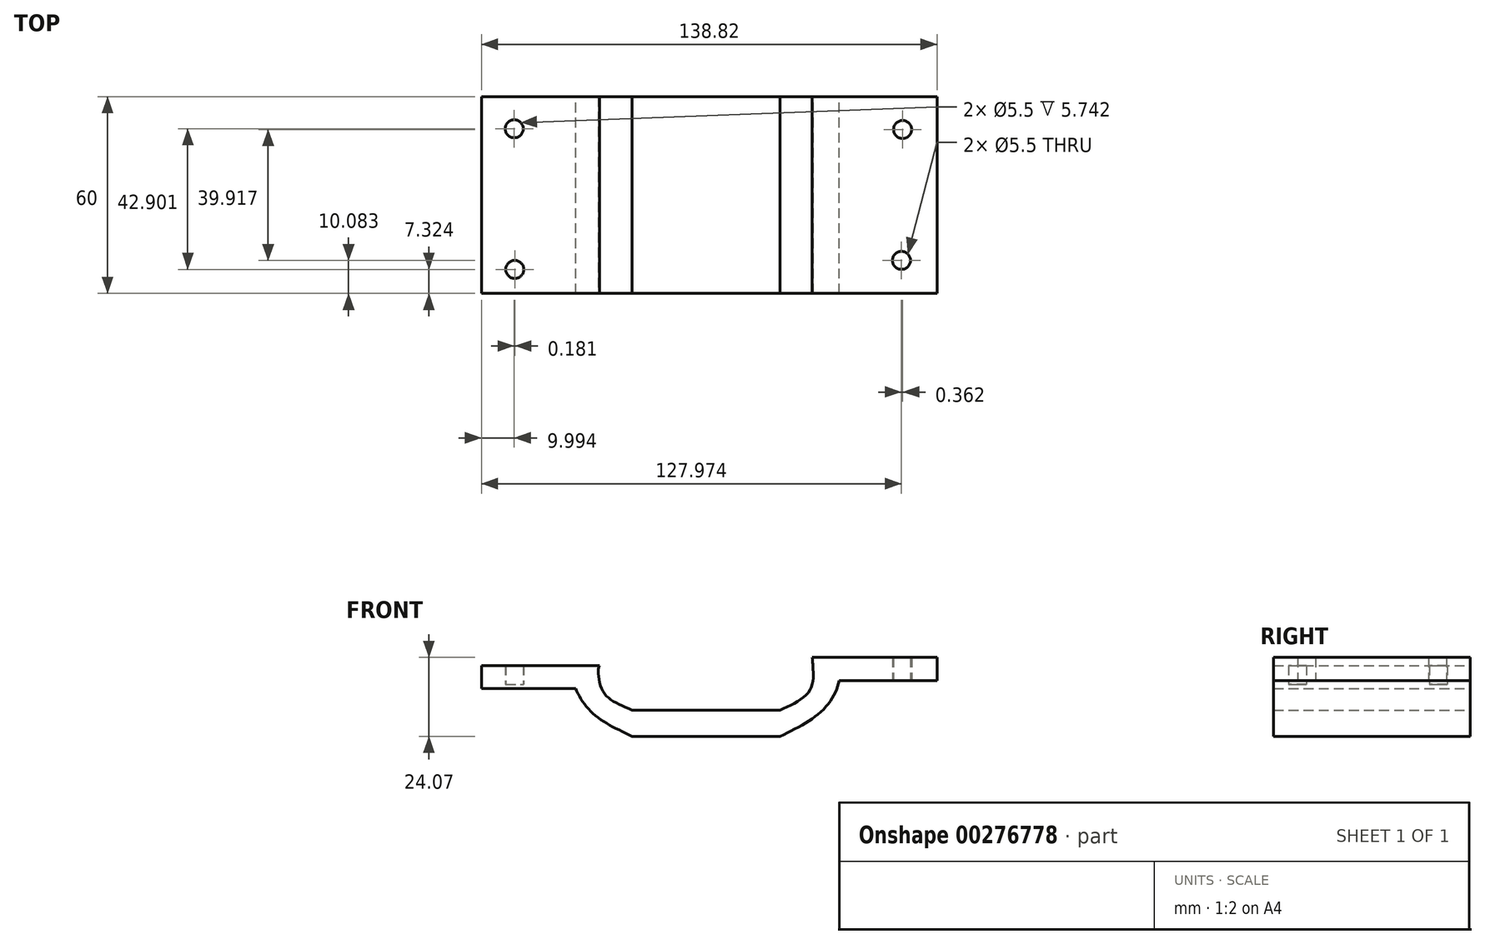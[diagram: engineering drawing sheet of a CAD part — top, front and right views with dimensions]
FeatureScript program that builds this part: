
annotation { "Feature Type Name" : "Feature", "Feature Type Description" : "" }
export const myFeature = defineFeature(function(context is Context, id is Id, definition is map)
    precondition{}
    {
        {
            var Q0;
            Q0=qCreatedBy(makeId("Front.planeOp"),FACE);
            var sketch = newSketch(context, id + "F0", { "sketchPlane" : qUnion([Q0])});
            skPoint(sketch, "E0.middle", {"position": v(20.36, 1.19) * mm});
            skLineSegment(sketch, "E1", {"start": v(-15.58, -15.88) * mm, "end": v(29.42, -15.88) * mm});
            skLineSegment(sketch, "E2", {"start": v(-25.58, 5.74) * mm, "end": v(-33.58, 5.74) * mm});
            skFitSpline(sketch, "E3", {"points": [v(-15.58, -15.88) * mm, v(-28.58, -7.88) * mm, v(-33.58, 1.19) * mm, v(-33.58, 5.74) * mm], "startDerivative": vector(-35.54, 17.11) * mm, "endDerivative": vector(2.54, 22.06) * mm});
            skFitSpline(sketch, "E4", {"points": [v(29.42, -15.88) * mm, v(42.42, -7.88) * mm, v(47.42, 1.19) * mm, v(47.28, 8.19) * mm], "startDerivative": vector(35.54, 17.11) * mm, "endDerivative": vector(-2.54, 22.06) * mm});
            skFitSpline(sketch, "E5", {"points": [v(-25.58, 5.74) * mm, v(-25.8, 5.24) * mm, v(-24.65, -1.83) * mm, v(-15.58, -7.88) * mm], "startDerivative": vector(-1.25, -8.06) * mm, "endDerivative": vector(24.82, -10.78) * mm});
            skLineSegment(sketch, "E6", {"start": v(47.28, 8.19) * mm, "end": v(39.28, 8.19) * mm});
            skFitSpline(sketch, "E7", {"points": [v(39.28, 8.19) * mm, v(39.5, 5.24) * mm, v(38.5, -1.83) * mm, v(29.42, -7.88) * mm], "startDerivative": vector(1.15, -8.05) * mm, "endDerivative": vector(-25.06, -10.75) * mm});
            skLineSegment(sketch, "E8", {"start": v(-15.58, -7.88) * mm, "end": v(29.42, -7.88) * mm});
            skLineSegment(sketch, "E9", {"start": v(47.28, 8.19) * mm, "end": v(77.28, 8.19) * mm});
            skLineSegment(sketch, "E10", {"start": v(77.28, 8.19) * mm, "end": v(77.28, 1.19) * mm});
            skLineSegment(sketch, "E11", {"start": v(77.28, 1.19) * mm, "end": v(47.42, 1.19) * mm});
            skLineSegment(sketch, "E12", {"start": v(-33.58, 5.74) * mm, "end": v(-61.54, 5.74) * mm});
            skLineSegment(sketch, "E13", {"start": v(-61.54, 5.74) * mm, "end": v(-61.54, -1.26) * mm});
            skLineSegment(sketch, "E14", {"start": v(-61.54, -1.26) * mm, "end": v(-32.82, -1.26) * mm});
            skLineSegment(sketch, "E15", {"start": v(-64.92, 5.46) * mm, "end": v(-64.92, -15.43) * mm});
            skSolve(sketch);
        }
        {
            var Q0;
            Q0 = qSketchRegion(id + "F0", true);
            extrude(context, id + "F1", {"entities" : qUnion([Q0]), "depth" : 60 * mm});
        }
        {
            var Q0;
            Q0=qCreatedBy(makeId("Top.planeOp"),FACE);
            var sketch = newSketch(context, id + "F2", { "sketchPlane" : qUnion([Q0])});
            skCircle(sketch, "E16", {"center": v(-51.55, -9.77) * mm, "radius": 3 * mm});
            skCircle(sketch, "E17", {"center": v(-51.37, -52.68) * mm, "radius": 3 * mm});
            skCircle(sketch, "E18", {"center": v(66.8, -10) * mm, "radius": 3 * mm});
            skCircle(sketch, "E19", {"center": v(66.43, -49.92) * mm, "radius": 3 * mm});
            skSolve(sketch);
        }
        {
            var Q0;
            Q0=sQuery(id+"F2.wireOp",VERTEX,"E19.center");
            var Q1;
            Q1=sQuery(id+"F2.wireOp",VERTEX,"E18.center");
            var Q2;
            Q2=sQuery(id+"F2.wireOp",VERTEX,"E16.center");
            var Q3;
            Q3=sQuery(id+"F2.wireOp",VERTEX,"E17.center");
            var Q4;
            Q4=makeQuery(id+"F1.opExtrude","SWEPT_BODY",BODY,{"disambiguationData":[OSD([sQuery(id+"F0.wireOp",EDGE,"E1"),sQuery(id+"F0.wireOp",EDGE,"E2"),sQuery(id+"F0.wireOp",EDGE,"E3"),sQuery(id+"F0.wireOp",EDGE,"E4"),sQuery(id+"F0.wireOp",EDGE,"E5"),sQuery(id+"F0.wireOp",EDGE,"E6"),sQuery(id+"F0.wireOp",EDGE,"E7"),sQuery(id+"F0.wireOp",EDGE,"E8"),sQuery(id+"F0.wireOp",EDGE,"E9"),sQuery(id+"F0.wireOp",EDGE,"E10"),sQuery(id+"F0.wireOp",EDGE,"E11"),sQuery(id+"F0.wireOp",EDGE,"E12"),sQuery(id+"F0.wireOp",EDGE,"E13"),sQuery(id+"F0.wireOp",EDGE,"E14")])]});
            hole(context, id + "F3", {"style" : HoleStyle.SIMPLE, "endStyle" : HoleEndStyle.THROUGH, "oppositeDirection" : true, "holeDiameter" : 5.5 * mm, "tappedDepth" : 12.7 * mm, "tapClearance" : 3, "locations" : qUnion([Q0, Q1, Q2, Q3]), "scope" : qUnion([Q4])});
        }
    });
